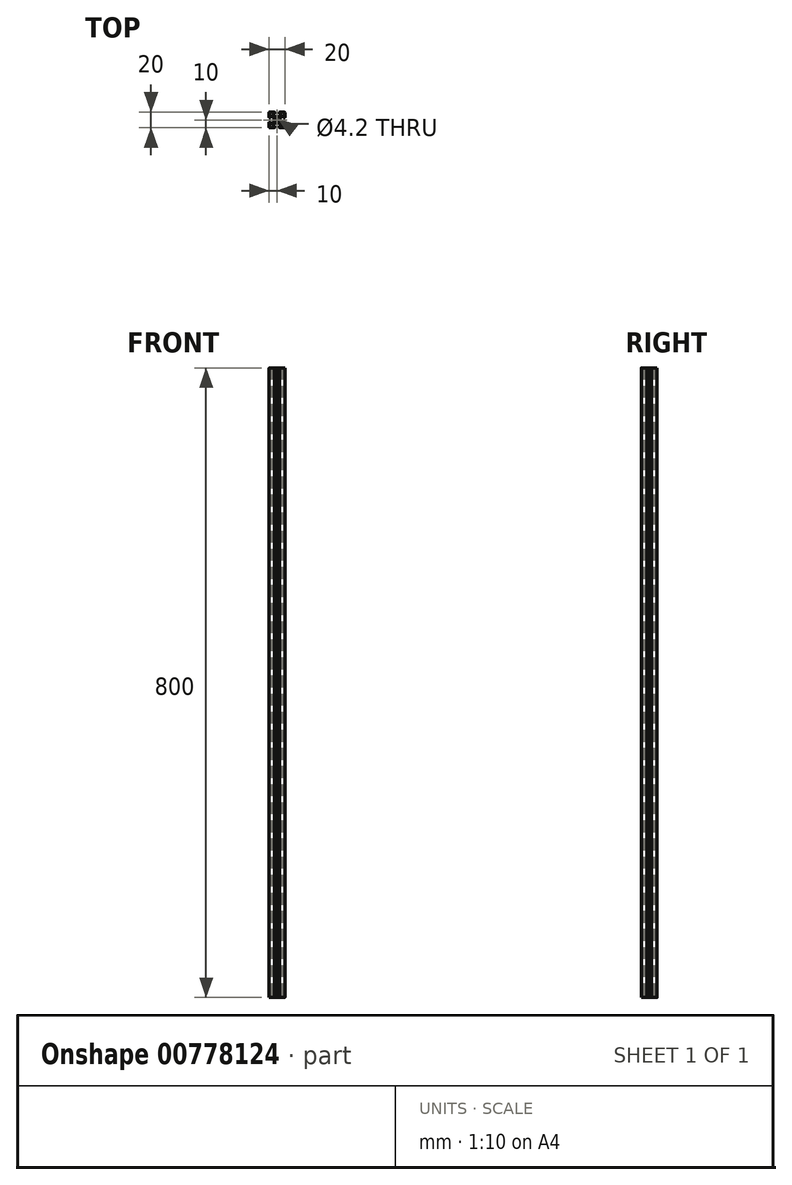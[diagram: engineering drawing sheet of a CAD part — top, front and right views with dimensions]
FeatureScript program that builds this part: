
annotation { "Feature Type Name" : "Feature", "Feature Type Description" : "" }
export const myFeature = defineFeature(function(context is Context, id is Id, definition is map)
    precondition{}
    {
        {
            assignVariable(context, id + "F0", {"name" : "length", "anyValue" : 800});
        }
        {
            var Q0;
            Q0=qCreatedBy(makeId("Top.planeOp"),FACE);
            var sketch = newSketch(context, id + "F1", { "sketchPlane" : qUnion([Q0])});
            skLineSegment(sketch, "E0", {"start": v(3, 8) * mm, "end": v(3, 10) * mm});
            skLineSegment(sketch, "E1", {"start": v(3, 10) * mm, "end": v(10, 10) * mm});
            skLineSegment(sketch, "E2", {"start": v(10, 10) * mm, "end": v(10, 3) * mm});
            skLineSegment(sketch, "E3", {"start": v(10, 3) * mm, "end": v(8, 3) * mm});
            skLineSegment(sketch, "E4", {"start": v(0, 4) * mm, "end": v(0, 8) * mm, "construction": true});
            skLineSegment(sketch, "E5", {"start": v(10, 0) * mm, "end": v(10, 3) * mm, "construction": true});
            skLineSegment(sketch, "E6", {"start": v(0, -1.05) * mm, "end": v(2.1, -1.05) * mm, "construction": true});
            skLineSegment(sketch, "E7", {"start": v(-1.94, 0) * mm, "end": v(-1.94, 2.1) * mm, "construction": true});
            skArc(sketch, "E8", {"start": v(2.1, 0) * mm, "mid": v(1.48, 1.48) * mm, "end": v(0, 2.1) * mm});
            skLineSegment(sketch, "E9", {"start": v(0.25, 4) * mm, "end": v(0, 3.75) * mm});
            skLineSegment(sketch, "E10", {"start": v(0.25, 4) * mm, "end": v(2.31, 4) * mm});
            skLineSegment(sketch, "E11", {"start": v(0, 3.75) * mm, "end": v(0, 0) * mm});
            skLineSegment(sketch, "E12", {"start": v(0.25, 4) * mm, "end": v(0.25, 3.75) * mm, "construction": true});
            skLineSegment(sketch, "E13", {"start": v(0.25, 3.75) * mm, "end": v(0, 3.75) * mm, "construction": true});
            skLineSegment(sketch, "E14", {"start": v(4, 0.25) * mm, "end": v(3.75, 0) * mm});
            skLineSegment(sketch, "E15", {"start": v(4, 0.25) * mm, "end": v(4, 2.31) * mm});
            skLineSegment(sketch, "E16", {"start": v(3.75, 0) * mm, "end": v(0, 0) * mm});
            skLineSegment(sketch, "E17", {"start": v(3.75, 0) * mm, "end": v(4, 0) * mm, "construction": true});
            skLineSegment(sketch, "E18", {"start": v(4, 0) * mm, "end": v(4, 0.25) * mm, "construction": true});
            skLineSegment(sketch, "E19", {"start": v(-2.52, 0) * mm, "end": v(-2.52, 4) * mm, "construction": true});
            skLineSegment(sketch, "E20", {"start": v(10, 11.57) * mm, "end": v(6, 11.57) * mm, "construction": true});
            skLineSegment(sketch, "E21", {"start": v(2.31, 4) * mm, "end": v(6, 7.69) * mm});
            skLineSegment(sketch, "E22", {"start": v(6, 7.69) * mm, "end": v(6, 8) * mm});
            skLineSegment(sketch, "E23", {"start": v(6, 8) * mm, "end": v(3, 8) * mm});
            skLineSegment(sketch, "E24", {"start": v(4, 2.31) * mm, "end": v(7.69, 6) * mm});
            skLineSegment(sketch, "E25", {"start": v(7.69, 6) * mm, "end": v(8, 6) * mm});
            skLineSegment(sketch, "E26", {"start": v(8, 6) * mm, "end": v(8, 3) * mm});
            skLineSegment(sketch, "E27", {"start": v(0, -2.77) * mm, "end": v(10, -2.77) * mm, "construction": true});
            skLineSegment(sketch, "E28", {"start": v(-4.38, 0) * mm, "end": v(-4.38, 10) * mm, "construction": true});
            skSolve(sketch);
        }
        {
            var Q0;
            Q0=makeQuery(id+"F1.imprint","IMPRINT",FACE,{"disambiguationData":[TD([[makeQuery(id+"F1.imprint","IMPRINT",EDGE,{"derivedFrom":sQuery(id+"F1.wireOp",EDGE,"E0")}),-1.0]])]});
            extrude(context, id + "F2", {"entities" : qUnion([Q0]), "depth" : (getVariable(context, 'length')) * mm, "offsetDistance" : 25 * mm});
        }
        {
            var Q0;
            Q0=makeQuery(id+"F2.opExtrude","SWEPT_FACE",FACE,{"disambiguationData":[OSD([sQuery(id+"F1.wireOp",EDGE,"E11")])]});
            var sketch = newSketch(context, id + "F3", { "sketchPlane" : qUnion([Q0])});
            skLineSegment(sketch, "E29", {"start": v(0, 0) * mm, "end": v(0, 800) * mm, "construction": true});
            skLineSegment(sketch, "E30", {"start": v(0, 0) * mm, "end": v(0, 0) * mm});
            skSolve(sketch);
        }
        {
            var Q0;
            Q0=makeQuery(id+"F2.opExtrude","SWEPT_EDGE",EDGE,{"disambiguationData":[OSD([sQuery(id+"F1.wireOp",EDGE,"Rf0Sl96Y-ScDn-mZ9m-LOWX-WQUDAtbnoyPT"),sQuery(id+"F1.wireOp",EDGE,"E0")])]});
            var Q1;
            Q1=makeQuery(id+"F2.opExtrude","SWEPT_EDGE",EDGE,{"disambiguationData":[OSD([sQuery(id+"F1.wireOp",EDGE,"E0"),sQuery(id+"F1.wireOp",EDGE,"E1")])]});
            var Q2;
            Q2=makeQuery(id+"F2.opExtrude","SWEPT_EDGE",EDGE,{"disambiguationData":[OSD([sQuery(id+"F1.wireOp",EDGE,"E3"),sQuery(id+"F1.wireOp",EDGE,"Eyhcc8HV-4kKn-JRNb-qOur-QaTbRjsZhEgT")])]});
            var Q3;
            Q3=makeQuery(id+"F2.opExtrude","SWEPT_EDGE",EDGE,{"disambiguationData":[OSD([sQuery(id+"F1.wireOp",EDGE,"E2"),sQuery(id+"F1.wireOp",EDGE,"E3")])]});
            fillet(context, id + "F4", {"entities" : qUnion([Q0, Q1, Q2, Q3]), "radius" : .5 * mm, "tangentPropagation" : true, "allowEdgeOverflow" : false});
        }
        {
            var Q0;
            Q0=makeQuery(id+"F2.opExtrude","SWEPT_EDGE",EDGE,{"disambiguationData":[OSD([sQuery(id+"F1.wireOp",EDGE,"E1"),sQuery(id+"F1.wireOp",EDGE,"E2")])]});
            fillet(context, id + "F5", {"entities" : qUnion([Q0]), "radius" : 1 * mm, "tangentPropagation" : true, "allowEdgeOverflow" : false});
        }
        {
            var Q0;
            Q0=makeQuery(id+"F2.opExtrude","SWEPT_BODY",BODY,{"disambiguationData":[OSD([sQuery(id+"F1.wireOp",EDGE,"9SJMXMo0-dkYv-twFB-hknK-kOqVDHcsv254"),sQuery(id+"F1.wireOp",EDGE,"o1RnQ2Ng-A66d-rHjm-PBcj-g4lrANHWvCor"),sQuery(id+"F1.wireOp",EDGE,"1mQT7SEN-KPz8-SMVO-awTg-AfnAztzVUNHk"),sQuery(id+"F1.wireOp",EDGE,"Rf0Sl96Y-ScDn-mZ9m-LOWX-WQUDAtbnoyPT"),sQuery(id+"F1.wireOp",EDGE,"E0"),sQuery(id+"F1.wireOp",EDGE,"E1"),sQuery(id+"F1.wireOp",EDGE,"E2"),sQuery(id+"F1.wireOp",EDGE,"E3"),sQuery(id+"F1.wireOp",EDGE,"Eyhcc8HV-4kKn-JRNb-qOur-QaTbRjsZhEgT"),sQuery(id+"F1.wireOp",EDGE,"95rPvxu8-eIL6-W2c8-GXrf-QxnVqfQWygFx"),sQuery(id+"F1.wireOp",EDGE,"WbT9Y7XW-Sjwo-79SY-Fnl1-x7dpX7sh3397"),sQuery(id+"F1.wireOp",EDGE,"Jte90sJ9-w5XJ-2fnf-bIyj-IUqkj70RDiN1"),sQuery(id+"F1.wireOp",EDGE,"E8")])]});
            var Q1;
            Q1=sQuery(id+"F3.wireOp",EDGE,"E29");
            circularPattern(context, id + "F6", {"operationType" : NewBodyOperationType.ADD, "entities" : qUnion([Q0]), "axis" : qUnion([Q1]), "angle" : 360 * degree, "instanceCount" : 4, "equalSpace" : true});
        }
    });
